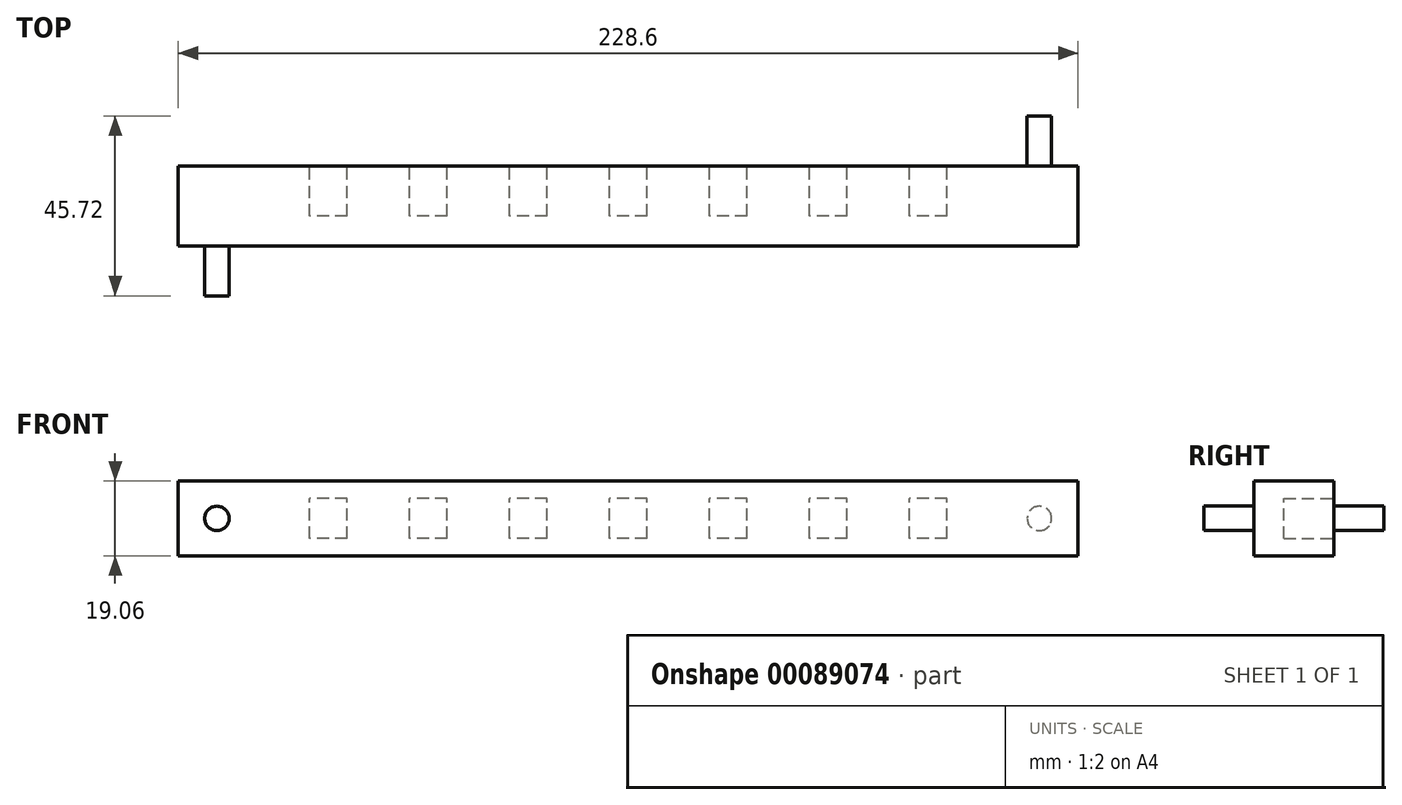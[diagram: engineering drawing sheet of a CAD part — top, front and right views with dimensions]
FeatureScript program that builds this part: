
annotation { "Feature Type Name" : "Feature", "Feature Type Description" : "" }
export const myFeature = defineFeature(function(context is Context, id is Id, definition is map)
    precondition{}
    {
        {
            var Q0;
            Q0=qCreatedBy(makeId("Front.planeOp"),FACE);
            var sketch = newSketch(context, id + "F0", { "sketchPlane" : qUnion([Q0])});
            skLineSegment(sketch, "E0.bottom", {"start": v(114.3, 9.53) * mm, "end": v(-114.3, 9.53) * mm});
            skLineSegment(sketch, "E0.top", {"start": v(114.3, -9.53) * mm, "end": v(-114.3, -9.53) * mm});
            skLineSegment(sketch, "E0.left", {"start": v(114.3, 9.53) * mm, "end": v(114.3, -9.52) * mm});
            skLineSegment(sketch, "E0.right", {"start": v(-114.3, 9.53) * mm, "end": v(-114.3, -9.52) * mm});
            skPoint(sketch, "E0.middle", {"position": v(0, 0) * mm});
            skSolve(sketch);
        }
        {
            var Q0;
            Q0 = qSketchRegion(id + "F0", true);
            extrude(context, id + "F1", {"entities" : qUnion([Q0]), "depth" : 20.32 * mm});
        }
        {
            var Q0;
            Q0=makeQuery(id+"F1.opExtrude","CAP_FACE",FACE,{"disambiguationData":[OSD([sQuery(id+"F0.wireOp",EDGE,"E0.bottom"),sQuery(id+"F0.wireOp",EDGE,"E0.top"),sQuery(id+"F0.wireOp",EDGE,"E0.left"),sQuery(id+"F0.wireOp",EDGE,"E0.right")])],"isStart":false});
            var sketch = newSketch(context, id + "F2", { "sketchPlane" : qUnion([Q0])});
            skCircle(sketch, "E1", {"center": v(-104.48, 0) * mm, "radius": 3.11 * mm});
            skSolve(sketch);
        }
        {
            var Q0;
            Q0=makeQuery(id+"F1.opExtrude","CAP_FACE",FACE,{"disambiguationData":[OSD([sQuery(id+"F0.wireOp",EDGE,"E0.bottom"),sQuery(id+"F0.wireOp",EDGE,"E0.top"),sQuery(id+"F0.wireOp",EDGE,"E0.left"),sQuery(id+"F0.wireOp",EDGE,"E0.right")])],"isStart":true});
            var sketch = newSketch(context, id + "F3", { "sketchPlane" : qUnion([Q0])});
            skLineSegment(sketch, "E2.bottom", {"start": v(-4.76, -5.08) * mm, "end": v(4.76, -5.08) * mm});
            skLineSegment(sketch, "E2.top", {"start": v(-4.76, 5.08) * mm, "end": v(4.76, 5.08) * mm});
            skLineSegment(sketch, "E2.left", {"start": v(-4.76, -5.08) * mm, "end": v(-4.76, 5.08) * mm});
            skLineSegment(sketch, "E2.right", {"start": v(4.76, -5.08) * mm, "end": v(4.76, 5.08) * mm});
            skPoint(sketch, "E2.middle", {"position": v(0, 0) * mm});
            skLineSegment(sketch, "E3.1.0.0", {"start": v(20.64, -5.08) * mm, "end": v(30.16, -5.08) * mm});
            skLineSegment(sketch, "E3.1.0.1", {"start": v(30.16, -5.08) * mm, "end": v(30.16, 5.08) * mm});
            skLineSegment(sketch, "E3.1.0.2", {"start": v(20.64, 5.08) * mm, "end": v(30.16, 5.08) * mm});
            skLineSegment(sketch, "E3.1.0.3", {"start": v(20.64, -5.08) * mm, "end": v(20.64, 5.08) * mm});
            skLineSegment(sketch, "E3.2.0.0", {"start": v(46.04, -5.08) * mm, "end": v(55.56, -5.08) * mm});
            skLineSegment(sketch, "E3.2.0.1", {"start": v(55.56, -5.08) * mm, "end": v(55.56, 5.08) * mm});
            skLineSegment(sketch, "E3.2.0.2", {"start": v(46.04, 5.08) * mm, "end": v(55.56, 5.08) * mm});
            skLineSegment(sketch, "E3.2.0.3", {"start": v(46.04, -5.08) * mm, "end": v(46.04, 5.08) * mm});
            skLineSegment(sketch, "E3.direction1", {"start": v(-4.76, -5.08) * mm, "end": v(20.64, -5.08) * mm, "construction": true});
            skLineSegment(sketch, "E4.1.0.0", {"start": v(-30.16, -5.08) * mm, "end": v(-20.64, -5.08) * mm});
            skLineSegment(sketch, "E4.1.0.1", {"start": v(-30.16, -5.08) * mm, "end": v(-30.16, 5.08) * mm});
            skLineSegment(sketch, "E4.1.0.2", {"start": v(-30.16, 5.08) * mm, "end": v(-20.64, 5.08) * mm});
            skLineSegment(sketch, "E4.1.0.3", {"start": v(-20.64, -5.08) * mm, "end": v(-20.64, 5.08) * mm});
            skLineSegment(sketch, "E4.2.0.0", {"start": v(-55.56, -5.08) * mm, "end": v(-46.04, -5.08) * mm});
            skLineSegment(sketch, "E4.2.0.1", {"start": v(-55.56, -5.08) * mm, "end": v(-55.56, 5.08) * mm});
            skLineSegment(sketch, "E4.2.0.2", {"start": v(-55.56, 5.08) * mm, "end": v(-46.04, 5.08) * mm});
            skLineSegment(sketch, "E4.2.0.3", {"start": v(-46.04, -5.08) * mm, "end": v(-46.04, 5.08) * mm});
            skLineSegment(sketch, "E4.2.0.4", {"start": v(-30.16, -5.08) * mm, "end": v(-20.64, -5.08) * mm});
            skLineSegment(sketch, "E4.direction1", {"start": v(-4.76, -5.08) * mm, "end": v(-30.16, -5.08) * mm, "construction": true});
            skLineSegment(sketch, "E5.0.3.0", {"start": v(-80.96, -5.08) * mm, "end": v(-71.44, -5.08) * mm});
            skLineSegment(sketch, "E5.3.3.0", {"start": v(-80.96, -5.08) * mm, "end": v(-80.96, 5.08) * mm});
            skLineSegment(sketch, "E5.6.3.0", {"start": v(-80.96, 5.08) * mm, "end": v(-71.44, 5.08) * mm});
            skLineSegment(sketch, "E5.9.3.0", {"start": v(-71.44, -5.08) * mm, "end": v(-71.44, 5.08) * mm});
            skLineSegment(sketch, "E6.0.3.0", {"start": v(71.44, -5.08) * mm, "end": v(80.96, -5.08) * mm});
            skLineSegment(sketch, "E6.3.3.0", {"start": v(80.96, -5.08) * mm, "end": v(80.96, 5.08) * mm});
            skLineSegment(sketch, "E6.6.3.0", {"start": v(71.44, 5.08) * mm, "end": v(80.96, 5.08) * mm});
            skLineSegment(sketch, "E6.9.3.0", {"start": v(71.44, -5.08) * mm, "end": v(71.44, 5.08) * mm});
            skSolve(sketch);
        }
        {
            var Q0;
            Q0 = qSketchRegion(id + "F3", true);
            extrude(context, id + "F4", {"entities" : qUnion([Q0]), "operationType" : NewBodyOperationType.REMOVE, "oppositeDirection" : true, "depth" : 12.7 * mm});
        }
        {
            var Q0;
            Q0=makeQuery(id+"F2.imprint","IMPRINT",FACE,{"disambiguationData":[TD([[makeQuery(id+"F2.imprint","IMPRINT",EDGE,{"derivedFrom":sQuery(id+"F2.wireOp",EDGE,"E1")}),1.0]])]});
            extrude(context, id + "F5", {"entities" : qUnion([Q0]), "operationType" : NewBodyOperationType.ADD, "depth" : 12.7 * mm});
        }
        {
            var Q0;
            Q0=makeQuery(id+"F1.opExtrude","CAP_FACE",FACE,{"disambiguationData":[OSD([sQuery(id+"F0.wireOp",EDGE,"E0.bottom"),sQuery(id+"F0.wireOp",EDGE,"E0.top"),sQuery(id+"F0.wireOp",EDGE,"E0.left"),sQuery(id+"F0.wireOp",EDGE,"E0.right")])],"isStart":true});
            var sketch = newSketch(context, id + "F6", { "sketchPlane" : qUnion([Q0])});
            skCircle(sketch, "E7", {"center": v(-104.48, 0) * mm, "radius": 3.11 * mm});
            skSolve(sketch);
        }
        {
            var Q0;
            Q0=makeQuery(id+"F6.imprint","IMPRINT",FACE,{"disambiguationData":[TD([[makeQuery(id+"F6.imprint","IMPRINT",EDGE,{"derivedFrom":sQuery(id+"F6.wireOp",EDGE,"E7")}),1.0]])]});
            extrude(context, id + "F7", {"entities" : qUnion([Q0]), "operationType" : NewBodyOperationType.ADD, "depth" : 12.7 * mm});
        }
    });
